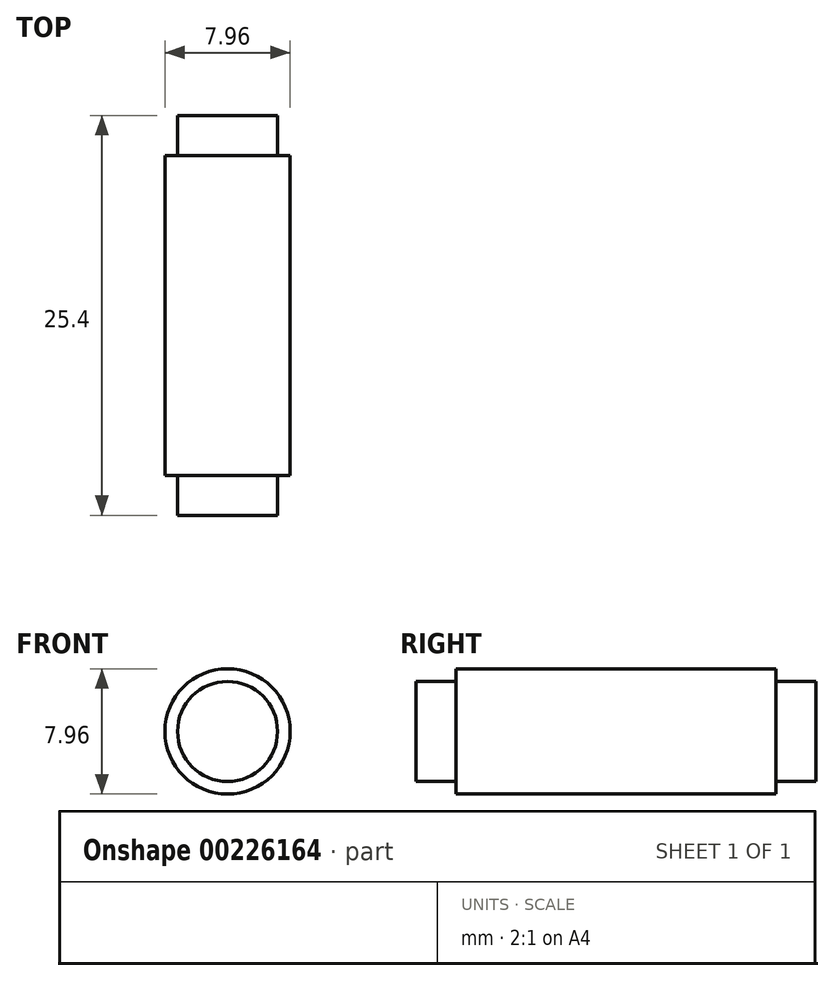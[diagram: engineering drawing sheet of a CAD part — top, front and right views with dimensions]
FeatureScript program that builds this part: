
annotation { "Feature Type Name" : "Feature", "Feature Type Description" : "" }
export const myFeature = defineFeature(function(context is Context, id is Id, definition is map)
    precondition{}
    {
        {
            var Q0;
            Q0=qCreatedBy(makeId("Front.planeOp"),FACE);
            var sketch = newSketch(context, id + "F0", { "sketchPlane" : qUnion([Q0])});
            skCircle(sketch, "E0", {"center": v(0, 0) * mm, "radius": 3.98 * mm});
            skSolve(sketch);
        }
        {
            var Q0;
            Q0 = qSketchRegion(id + "F0", true);
            extrude(context, id + "F1", {"entities" : qUnion([Q0]), "depth" : 25.4 * mm});
        }
        {
            var Q0;
            Q0=makeQuery(id+"F1.opExtrude","CAP_FACE",FACE,{"disambiguationData":[OSD([sQuery(id+"F0.wireOp",EDGE,"E0")])],"isStart":false});
            var sketch = newSketch(context, id + "F2", { "sketchPlane" : qUnion([Q0])});
            skCircle(sketch, "E1", {"center": v(0, 0) * mm, "radius": 3.98 * mm});
            skCircle(sketch, "E2", {"center": v(0, 0) * mm, "radius": 3.18 * mm});
            skSolve(sketch);
        }
        {
            var Q0;
            Q0 = qSketchRegion(id + "F2", true);
            extrude(context, id + "F3", {"entities" : qUnion([Q0]), "operationType" : NewBodyOperationType.REMOVE, "oppositeDirection" : true, "depth" : 2.54 * mm});
        }
        {
            var Q0;
            Q0=qCreatedBy(makeId("Front.planeOp"),FACE);
            var sketch = newSketch(context, id + "F4", { "sketchPlane" : qUnion([Q0])});
            skCircle(sketch, "E3", {"center": v(0, 0) * mm, "radius": 3.98 * mm});
            skCircle(sketch, "E4", {"center": v(0, 0) * mm, "radius": 3.18 * mm});
            skSolve(sketch);
        }
        {
            var Q0;
            Q0 = qSketchRegion(id + "F4", true);
            extrude(context, id + "F5", {"entities" : qUnion([Q0]), "operationType" : NewBodyOperationType.REMOVE, "depth" : 2.54 * mm});
        }
    });
